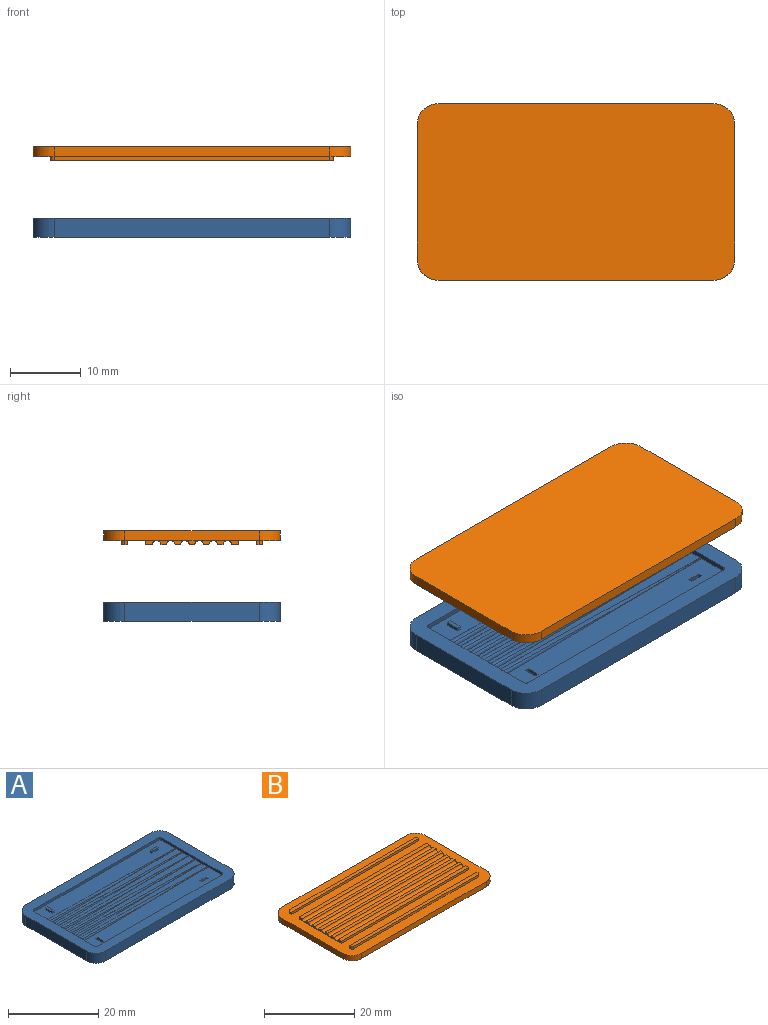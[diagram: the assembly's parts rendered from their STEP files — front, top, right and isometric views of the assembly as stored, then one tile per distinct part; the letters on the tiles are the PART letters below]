
ASSEMBLY  parts=2 mates=1
PART A: 63 faces, bbox 45x25x2.7 mm
  f0: plane 19x0.7mm, normal (1,0,0), area 9.9mm2, adj f1,f2,f3,f4,f5,f6,f7,f17
  f1: plane 40x1.8mm, normal (0,0,1), area 49.6mm2, adj f0,f21,f39,f40
  f2: plane 40x4.9mm, normal (0,0,1), area 182.3mm2, adj f0,f17,f21,f22,f23,f42,f53,f54
  f3: plane 40x1.8mm, normal (0,0,1), area 49.6mm2, adj f0,f21,f36,f37
  f4: plane 40x1.8mm, normal (0,0,1), area 49.6mm2, adj f0,f21,f33,f34
  f5: plane 40x1.8mm, normal (0,0,1), area 49.6mm2, adj f0,f21,f30,f31
  f6: plane 40x1.8mm, normal (0,0,1), area 49.6mm2, adj f0,f21,f27,f28
  f7: plane 40x4.9mm, normal (0,0,1), area 182.3mm2, adj f0,f18,f19,f20,f21,f25,f43,f44
  f8: plane 39x2.7mm, normal (0,-1,0), area 105.3mm2, adj f9,f15,f16,f24
  f9: cylinder r=3mm len=3mm, axis (0,0,1), area 12.7mm2, adj f8,f10,f16,f24
  f10: plane 19x2.7mm, normal (1,0,0), area 51.3mm2, adj f9,f11,f16,f24
  f11: cylinder r=3mm len=3mm, axis (0,0,1), area 12.7mm2, adj f10,f12,f16,f24
  f12: plane 39x2.7mm, normal (0,1,0), area 105.3mm2, adj f11,f13,f16,f24
  f13: cylinder r=3mm len=3mm, axis (0,0,1), area 12.7mm2, adj f12,f14,f16,f24
  f14: plane 19x2.7mm, normal (-1,0,0), area 51.3mm2, adj f13,f15,f16,f24
  f15: cylinder r=3mm len=3mm, axis (0,0,1), area 12.7mm2, adj f8,f14,f16,f24
  f16: plane 45x25mm, normal (0,0,-1), area 1117.3mm2, adj f8,f9,f10,f11,f12,f13,f14,f15
  f17: cylinder r=0.5mm len=0.7mm, axis (0,0,-1), area 0.5mm2, adj f0,f2,f23,f24
  f18: cylinder r=0.5mm len=0.7mm, axis (0,0,-1), area 0.5mm2, adj f0,f7,f19,f24
  f19: plane 39x0.7mm, normal (0,-1,0), area 27.3mm2, adj f7,f18,f20,f24
  f20: cylinder r=0.5mm len=0.7mm, axis (0,0,-1), area 0.5mm2, adj f7,f19,f21,f24
  f21: plane 19x0.7mm, normal (-1,0,0), area 13.2mm2, adj f1,f2,f3,f4,f5,f6,f7,f20
  f22: cylinder r=0.5mm len=0.7mm, axis (0,0,-1), area 0.5mm2, adj f2,f21,f23,f24
  f23: plane 39x0.7mm, normal (0,1,0), area 27.3mm2, adj f2,f17,f22,f24
  f24: plane 45x25mm, normal (0,0,1), area 317.5mm2, adj f0,f8,f9,f10,f11,f12,f13,f14
  f25: bspline ~40x0.5mm, area 9.8mm2, adj f0,f7,f21,f26
  f26: bspline ~40x0.98mm, area 26.7mm2, adj f0,f21,f25,f27
  f27: bspline ~40x0.5mm, area 9.8mm2, adj f0,f6,f21,f26
  f28: bspline ~40x0.5mm, area 9.8mm2, adj f0,f6,f21,f29
  f29: bspline ~40x0.98mm, area 26.7mm2, adj f0,f21,f28,f30
  f30: bspline ~40x0.5mm, area 9.8mm2, adj f0,f5,f21,f29
  f31: bspline ~40x0.5mm, area 9.8mm2, adj f0,f5,f21,f32
  f32: bspline ~40x0.98mm, area 26.7mm2, adj f0,f21,f31,f33
  f33: bspline ~40x0.5mm, area 9.8mm2, adj f0,f4,f21,f32
  f34: bspline ~40x0.5mm, area 9.8mm2, adj f0,f4,f21,f35
  f35: bspline ~40x0.98mm, area 26.7mm2, adj f0,f21,f34,f36
  f36: bspline ~40x0.5mm, area 9.8mm2, adj f0,f3,f21,f35
  f37: bspline ~40x0.5mm, area 9.8mm2, adj f0,f3,f21,f38
  f38: bspline ~40x0.98mm, area 26.7mm2, adj f0,f21,f37,f39
  f39: bspline ~40x0.5mm, area 9.8mm2, adj f0,f1,f21,f38
  f40: bspline ~40x0.5mm, area 9.8mm2, adj f0,f1,f21,f41
  f41: bspline ~40x0.98mm, area 26.7mm2, adj f0,f21,f40,f42
  f42: bspline ~40x0.5mm, area 9.8mm2, adj f0,f2,f21,f41
  f43: plane 0.6x0.5mm, normal (0,1,0), area 0.3mm2, adj f7,f44,f46,f47
  f44: plane 2x0.5mm, normal (-1,0,0), area 1mm2, adj f7,f43,f45,f47
  f45: plane 0.6x0.5mm, normal (0,-1,0), area 0.3mm2, adj f7,f44,f46,f47
  f46: plane 2x0.5mm, normal (1,0,0), area 1mm2, adj f7,f43,f45,f47
  f47: plane 2x0.6mm, normal (0,0,1), area 1.2mm2, adj f43,f44,f45,f46
  f48: plane 0.6x0.5mm, normal (1,0,0), area 0.3mm2, adj f7,f49,f51,f52
  f49: plane 2x0.5mm, normal (0,1,0), area 1mm2, adj f7,f48,f50,f52
  f50: plane 0.6x0.5mm, normal (-1,0,0), area 0.3mm2, adj f7,f49,f51,f52
  f51: plane 2x0.5mm, normal (0,-1,0), area 1mm2, adj f7,f48,f50,f52
  f52: plane 2x0.6mm, normal (0,0,1), area 1.2mm2, adj f48,f49,f50,f51
  f53: plane 0.6x0.5mm, normal (-1,0,0), area 0.3mm2, adj f2,f54,f56,f57
  f54: plane 2x0.5mm, normal (0,-1,0), area 1mm2, adj f2,f53,f55,f57
  f55: plane 0.6x0.5mm, normal (1,0,0), area 0.3mm2, adj f2,f54,f56,f57
  f56: plane 2x0.5mm, normal (0,1,0), area 1mm2, adj f2,f53,f55,f57
  f57: plane 2x0.6mm, normal (0,0,1), area 1.2mm2, adj f53,f54,f55,f56
  f58: plane 0.6x0.5mm, normal (0,1,0), area 0.3mm2, adj f2,f59,f61,f62
  f59: plane 2x0.5mm, normal (-1,0,0), area 1mm2, adj f2,f58,f60,f62
  f60: plane 0.6x0.5mm, normal (0,-1,0), area 0.3mm2, adj f2,f59,f61,f62
  f61: plane 2x0.5mm, normal (1,0,0), area 1mm2, adj f2,f58,f60,f62
  f62: plane 2x0.6mm, normal (0,0,1), area 1.2mm2, adj f58,f59,f60,f61
PART B: 53 faces, bbox 45x25x2 mm
  f0: plane 1.6x0.6mm, normal (-1,0,0), area 0.7mm2, adj f2,f40,f48,f52
  f1: plane 0.6x0.4mm, normal (1,0,0), area 0.2mm2, adj f34,f40,f41,f51
  f2: plane 40x1mm, normal (0,0,1), area 40mm2, adj f0,f32,f48,f52
  f3: plane 1.6x0.6mm, normal (1,0,0), area 0.7mm2, adj f40,f42,f43,f49
  f4: plane 0.6x0.4mm, normal (-1,0,0), area 0.2mm2, adj f5,f37,f40,f50
  f5: plane 40x0.9mm, normal (0,0,1), area 35.9mm2, adj f4,f31,f37,f38,f39,f50
  f6: plane 40x0.8mm, normal (0,0,1), area 32mm2, adj f7,f9,f47,f48
  f7: plane 2x0.6mm, normal (-1,0,0), area 0.6mm2, adj f6,f40,f47,f48
  f8: plane 0.6x0.4mm, normal (-1,0,0), area 0.2mm2, adj f36,f40,f41,f51
  f9: plane 2x0.6mm, normal (1,0,0), area 0.6mm2, adj f6,f40,f47,f48
  f10: plane 40x0.8mm, normal (0,0,1), area 32mm2, adj f11,f12,f46,f47
  f11: plane 2x0.6mm, normal (-1,0,0), area 0.6mm2, adj f10,f40,f46,f47
  f12: plane 2x0.6mm, normal (1,0,0), area 0.6mm2, adj f10,f40,f46,f47
  f13: plane 40x0.8mm, normal (0,0,1), area 32mm2, adj f14,f15,f45,f46
  f14: plane 2x0.6mm, normal (-1,0,0), area 0.6mm2, adj f13,f40,f45,f46
  f15: plane 2x0.6mm, normal (1,0,0), area 0.6mm2, adj f13,f40,f45,f46
  f16: plane 40x0.8mm, normal (0,0,1), area 32mm2, adj f17,f18,f44,f45
  f17: plane 2x0.6mm, normal (-1,0,0), area 0.6mm2, adj f16,f40,f44,f45
  f18: plane 2x0.6mm, normal (1,0,0), area 0.6mm2, adj f16,f40,f44,f45
  f19: plane 40x0.8mm, normal (0,0,1), area 32mm2, adj f20,f21,f43,f44
  f20: plane 2x0.6mm, normal (1,0,0), area 0.6mm2, adj f19,f40,f43,f44
  f21: plane 2x0.6mm, normal (-1,0,0), area 0.6mm2, adj f19,f40,f43,f44
  f22: plane 39x1.4mm, normal (0,-1,0), area 54.6mm2, adj f23,f29,f30,f40
  f23: cylinder r=3mm len=3mm, axis (0,0,1), area 6.6mm2, adj f22,f24,f30,f40
  f24: plane 19x1.4mm, normal (1,0,0), area 26.6mm2, adj f23,f25,f30,f40
  f25: cylinder r=3mm len=3mm, axis (0,0,1), area 6.6mm2, adj f24,f26,f30,f40
  f26: plane 39x1.4mm, normal (0,1,0), area 54.6mm2, adj f25,f27,f30,f40
  f27: cylinder r=3mm len=3mm, axis (0,0,1), area 6.6mm2, adj f26,f28,f30,f40
  f28: plane 19x1.4mm, normal (-1,0,0), area 26.6mm2, adj f27,f29,f30,f40
  f29: cylinder r=3mm len=3mm, axis (0,0,1), area 6.6mm2, adj f22,f28,f30,f40
  f30: plane 45x25mm, normal (0,0,-1), area 1117.3mm2, adj f22,f23,f24,f25,f26,f27,f28,f29
  f31: plane 0.6x0.4mm, normal (1,0,0), area 0.2mm2, adj f5,f39,f40,f50
  f32: plane 1.6x0.6mm, normal (1,0,0), area 0.7mm2, adj f2,f40,f48,f52
  f33: plane 1.6x0.6mm, normal (-1,0,0), area 0.7mm2, adj f40,f42,f43,f49
  f34: cylinder r=0.5mm len=0.6mm, axis (0,0,1), area 0.5mm2, adj f1,f35,f40,f41
  f35: plane 39x0.6mm, normal (0,-1,0), area 23.4mm2, adj f34,f36,f40,f41
  f36: cylinder r=0.5mm len=0.6mm, axis (0,0,1), area 0.5mm2, adj f8,f35,f40,f41
  f37: cylinder r=0.5mm len=0.6mm, axis (0,0,1), area 0.5mm2, adj f4,f5,f38,f40
  f38: plane 39x0.6mm, normal (0,1,0), area 23.4mm2, adj f5,f37,f39,f40
  f39: cylinder r=0.5mm len=0.6mm, axis (0,0,1), area 0.5mm2, adj f5,f31,f38,f40
  f40: plane 45x25mm, normal (0,0,1), area 517.5mm2, adj f0,f1,f3,f4,f7,f8,f9,f11
  f41: plane 40x0.9mm, normal (0,0,1), area 35.9mm2, adj f1,f8,f34,f35,f36,f51
  f42: plane 40x1mm, normal (0,0,1), area 40mm2, adj f3,f33,f43,f49
  f43: cylinder r=0.6mm len=40mm, axis (1,0,0), area 75.4mm2, adj f3,f19,f20,f21,f33,f42
  f44: cylinder r=0.6mm len=40mm, axis (1,0,0), area 75.4mm2, adj f16,f17,f18,f19,f20,f21
  f45: cylinder r=0.6mm len=40mm, axis (1,0,0), area 75.4mm2, adj f13,f14,f15,f16,f17,f18
  f46: cylinder r=0.6mm len=40mm, axis (1,0,0), area 75.4mm2, adj f10,f11,f12,f13,f14,f15
  f47: cylinder r=0.6mm len=40mm, axis (1,0,0), area 75.4mm2, adj f6,f7,f9,f10,f11,f12
  f48: cylinder r=0.6mm len=40mm, axis (1,0,0), area 75.4mm2, adj f0,f2,f6,f7,f9,f32
  f49: plane 40x0.6mm, normal (0,1,0), area 24mm2, adj f3,f33,f40,f42
  f50: plane 40x0.6mm, normal (0,-1,0), area 24mm2, adj f4,f5,f31,f40
  f51: plane 40x0.6mm, normal (0,1,0), area 24mm2, adj f1,f8,f40,f41
  f52: plane 40x0.6mm, normal (0,-1,0), area 24mm2, adj f0,f2,f32,f40
PLACE A t=(6.92,-2.48,3.97)mm fixed
PLACE B rot(axis=(0,1,0),180deg) t=(6.92,-2.48,12.81)mm
MATE slider B.f40 <-> A.f24  axis (0,0,-1) through (-12.58,-14.98,13.41)mm
